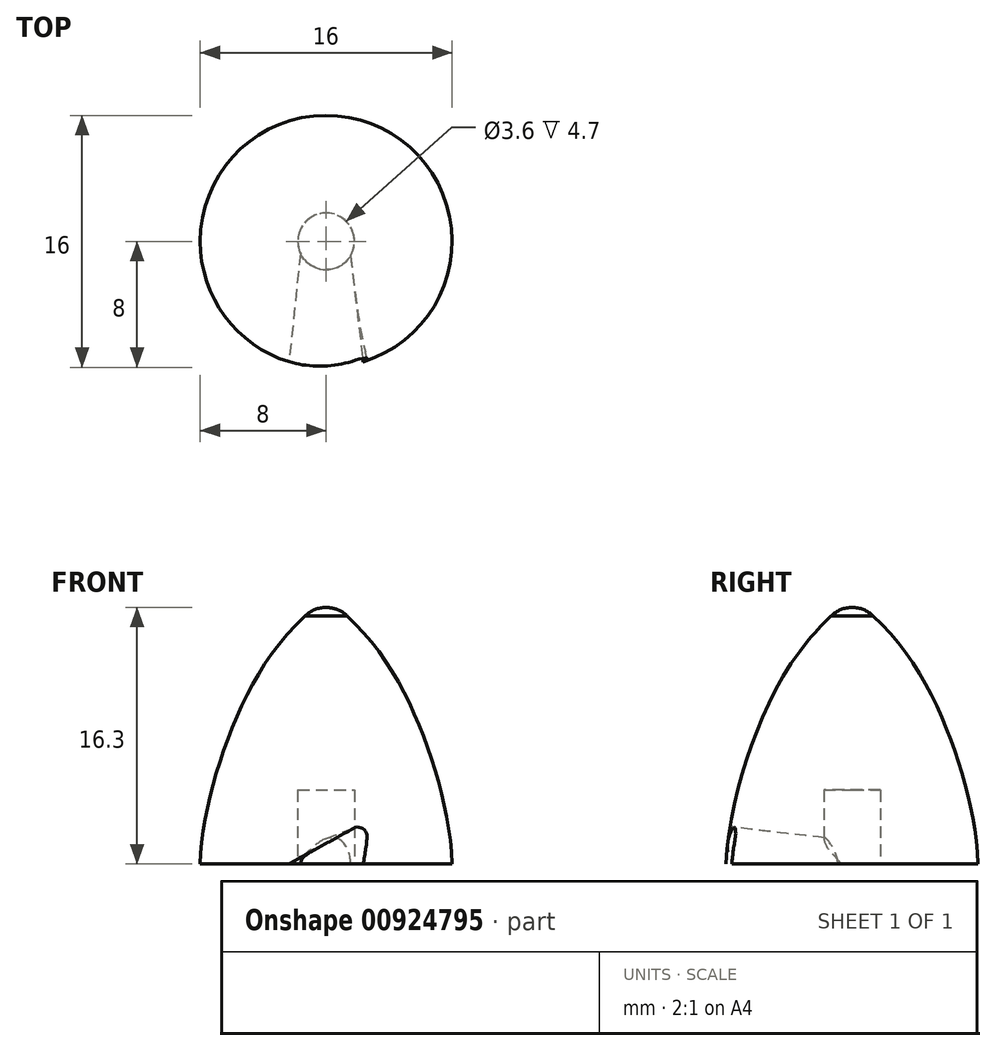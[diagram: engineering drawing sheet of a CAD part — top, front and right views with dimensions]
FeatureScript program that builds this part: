
annotation { "Feature Type Name" : "Feature", "Feature Type Description" : "" }
export const myFeature = defineFeature(function(context is Context, id is Id, definition is map)
    precondition{}
    {
        {
            var Q0;
            Q0=qCreatedBy(makeId("Front.planeOp"),FACE);
            var sketch = newSketch(context, id + "F0", { "sketchPlane" : qUnion([Q0])});
            skFitSpline(sketch, "E0", {"points": [v(-8, 0) * mm, v(-5.92, 8.78) * mm, v(0, 16.92) * mm], "startDerivative": vector(0.53, 17) * mm, "endDerivative": vector(17.9, 14.1) * mm});
            skLineSegment(sketch, "E1", {"start": v(-8, 0) * mm, "end": v(0, 0) * mm});
            skLineSegment(sketch, "E2", {"start": v(0, 0) * mm, "end": v(0, 16.3) * mm});
            skArc(sketch, "E3", {"start": v(0, 16.3) * mm, "mid": v(-0.72, 16.16) * mm, "end": v(-1.33, 15.77) * mm});
            skSolve(sketch);
        }
        {
            var Q0;
            Q0=makeQuery(id+"F0.imprint","IMPRINT",FACE,{"disambiguationData":[TD([[makeQuery(id+"F0.imprint","IMPRINT",EDGE,{"derivedFrom":sQuery(id+"F0.wireOp",EDGE,"E0")}),-1.0]])]});
            var Q1;
            Q1=sQuery(id+"F0.wireOp",EDGE,"E2");
            revolve(context, id + "F1", {"surfaceOperationType" : NewSurfaceOperationType.NEW, "entities" : qUnion([Q0]), "axis" : qUnion([Q1]), "revolveType" : RevolveType.FULL});
        }
        {
            var Q0;
            Q0=makeQuery(id+"F1.opRevolve","SWEPT_FACE",FACE,{"disambiguationData":[OSD([sQuery(id+"F0.wireOp",EDGE,"E1")])]});
            var sketch = newSketch(context, id + "F2", { "sketchPlane" : qUnion([Q0])});
            skCircle(sketch, "E4", {"center": v(0, 0) * mm, "radius": 1.8 * mm});
            skSolve(sketch);
        }
        {
            var Q0;
            Q0=makeQuery(id+"F2.imprint","IMPRINT",FACE,{"disambiguationData":[TD([[makeQuery(id+"F2.imprint","IMPRINT",EDGE,{"derivedFrom":sQuery(id+"F2.wireOp",EDGE,"E4")}),1.0]])]});
            extrude(context, id + "F3", {"entities" : qUnion([Q0]), "operationType" : NewBodyOperationType.REMOVE, "oppositeDirection" : true, "depth" : 4.7 * mm, "offsetDistance" : 25 * mm});
        }
        {
            var Q0;
            Q0=qCreatedBy(makeId("Front.planeOp"),FACE);
            cPlane(context, id + "F4", {"entities" : qUnion([Q0]), "cplaneType" : CPlaneType.OFFSET, "offset" : 9 * mm, "width" : 150 * mm, "height" : 150 * mm});
        }
        {
            var Q0;
            Q0=qCreatedBy(id+"F4.planeOp",FACE);
            var sketch = newSketch(context, id + "F5", { "sketchPlane" : qUnion([Q0])});
            skLineSegment(sketch, "E5", {"start": v(-2.5, 0) * mm, "end": v(-3, 1.91) * mm, "construction": true});
            skLineSegment(sketch, "E6", {"start": v(-2.29, 2.48) * mm, "end": v(2.5, 0) * mm, "construction": true});
            skLineSegment(sketch, "E7", {"start": v(2.5, 0) * mm, "end": v(-2.5, 0) * mm});
            skPoint(sketch, "E8.visualSharp", {"position": v(-3.28, 3) * mm});
            skArc(sketch, "E8.filletArc", {"start": v(-2.29, 2.48) * mm, "mid": v(-2.83, 2.43) * mm, "end": v(-3, 1.91) * mm, "construction": true});
            skLineSegment(sketch, "E9.MirrorCS", {"start": v(2.5, 0) * mm, "end": v(3, 1.91) * mm});
            skArc(sketch, "E10.MirrorCS", {"start": v(2.29, 2.48) * mm, "mid": v(2.83, 2.43) * mm, "end": v(3, 1.91) * mm});
            skLineSegment(sketch, "E11.MirrorCS", {"start": v(2.29, 2.48) * mm, "end": v(-2.5, 0) * mm});
            skSolve(sketch);
        }
        {
            var Q0;
            Q0=qCreatedBy(makeId("Front.planeOp"),FACE);
            var sketch = newSketch(context, id + "F6", { "sketchPlane" : qUnion([Q0])});
            skArc(sketch, "E12", {"start": v(1.45, 0) * mm, "mid": v(-0.05, 1.5) * mm, "end": v(-1.55, 0) * mm});
            skLineSegment(sketch, "E13", {"start": v(-1.55, 0) * mm, "end": v(1.45, 0) * mm});
            skSolve(sketch);
        }
        {
            var Q1;
            Q1=makeQuery(id+"F6.imprint","IMPRINT",FACE,{"disambiguationData":[TD([[makeQuery(id+"F6.imprint","IMPRINT",EDGE,{"derivedFrom":sQuery(id+"F6.wireOp",EDGE,"E12")}),1.0]])]});
            var Q2;
            Q2=makeQuery(id+"F5.imprint","IMPRINT",FACE,{"disambiguationData":[TD([[makeQuery(id+"F5.imprint","IMPRINT",EDGE,{"derivedFrom":sQuery(id+"F5.wireOp",EDGE,"E7")}),-1.0]])]});
            loft(context, id + "F7", {"operationType" : NewBodyOperationType.REMOVE, "sheetProfilesArray" : [{ "sheetProfileEntities" : qUnion([Q1]) }, { "sheetProfileEntities" : qUnion([Q2]) }]});
        }
    });
